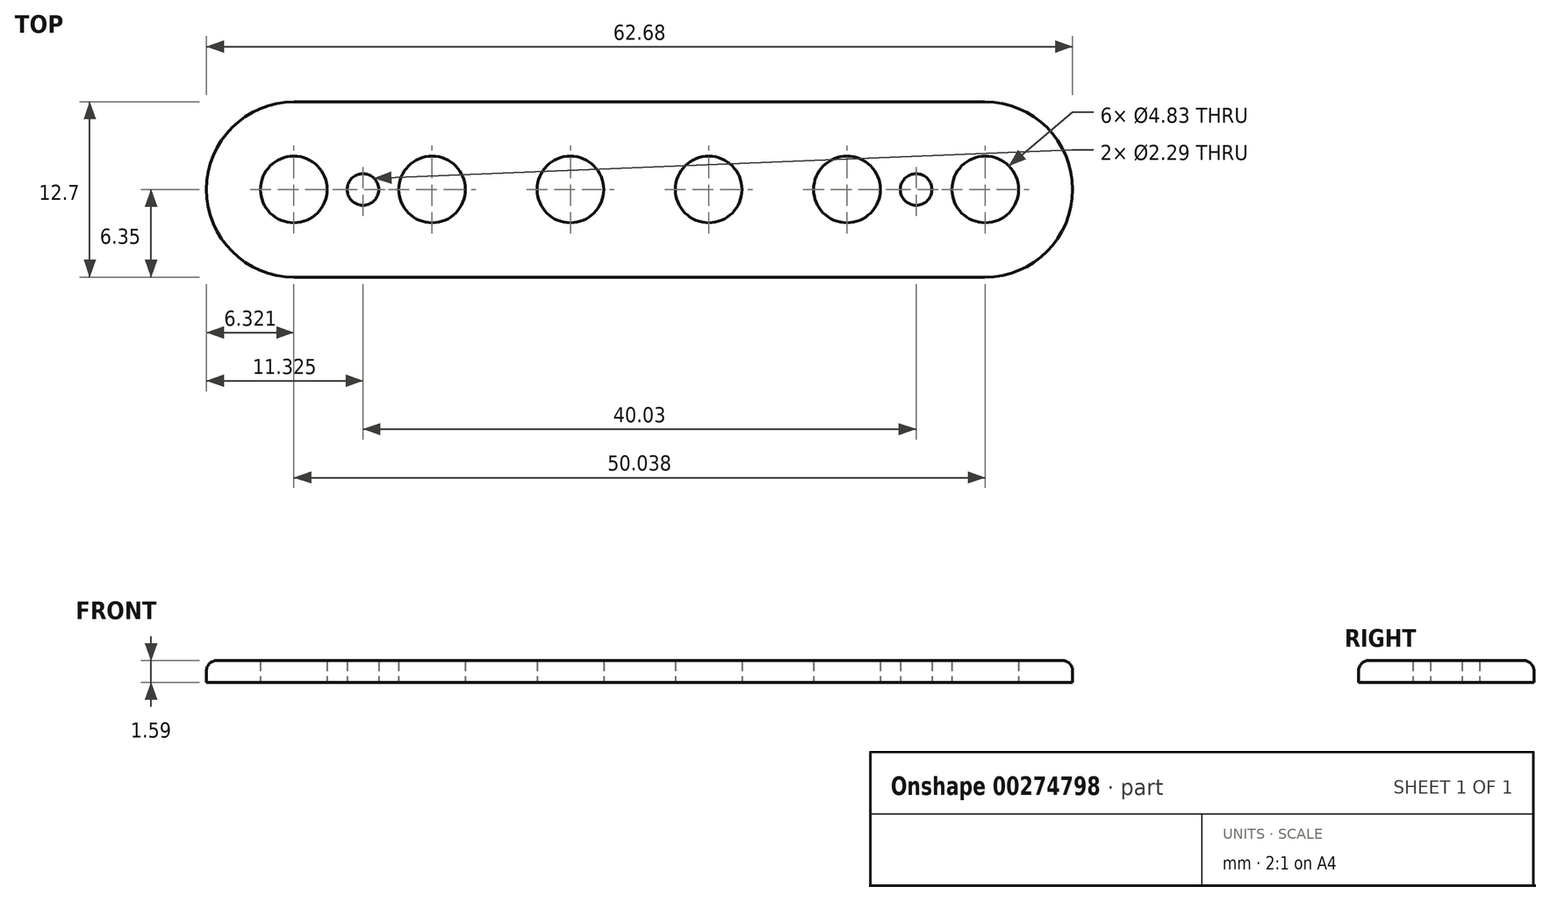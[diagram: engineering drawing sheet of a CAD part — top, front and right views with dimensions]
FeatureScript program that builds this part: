
annotation { "Feature Type Name" : "Feature", "Feature Type Description" : "" }
export const myFeature = defineFeature(function(context is Context, id is Id, definition is map)
    precondition{}
    {
        {
            var Q0;
            Q0=qCreatedBy(makeId("Top.planeOp"),FACE);
            var sketch = newSketch(context, id + "F0", { "sketchPlane" : qUnion([Q0])});
            skLineSegment(sketch, "E0", {"start": v(0, 0) * mm, "end": v(31.34, 0) * mm, "construction": true});
            skLineSegment(sketch, "E1.0", {"start": v(0, 6.35) * mm, "end": v(25, 6.35) * mm});
            skCircle(sketch, "E2", {"center": v(5, 0) * mm, "radius": 2.41 * mm});
            skCircle(sketch, "E3.1.0.0", {"center": v(15.01, 0) * mm, "radius": 2.41 * mm});
            skCircle(sketch, "E3.2.0.0", {"center": v(25.02, 0) * mm, "radius": 2.41 * mm});
            skLineSegment(sketch, "E3.direction1", {"start": v(5, 0) * mm, "end": v(15.01, 0) * mm, "construction": true});
            skLineSegment(sketch, "E4.MirrorCS", {"start": v(0, -6.35) * mm, "end": v(25, -6.35) * mm});
            skArc(sketch, "E5", {"start": v(25, -6.35) * mm, "mid": v(31.34, 0) * mm, "end": v(25, 6.35) * mm});
            skLineSegment(sketch, "E6.MirrorCS", {"start": v(0, 6.35) * mm, "end": v(-25, 6.35) * mm});
            skArc(sketch, "E7.MirrorCS", {"start": v(-25, -6.35) * mm, "mid": v(-31.34, 0) * mm, "end": v(-25, 6.35) * mm});
            skCircle(sketch, "E8.MirrorC", {"center": v(-5, 0) * mm, "radius": 2.41 * mm});
            skCircle(sketch, "E9.MirrorC", {"center": v(-25.02, 0) * mm, "radius": 2.41 * mm});
            skLineSegment(sketch, "E10.MirrorCS", {"start": v(-5, 0) * mm, "end": v(-15.01, 0) * mm, "construction": true});
            skLineSegment(sketch, "E11.MirrorCS", {"start": v(0, 0) * mm, "end": v(-31.34, 0) * mm, "construction": true});
            skCircle(sketch, "E12.MirrorC", {"center": v(-15.01, 0) * mm, "radius": 2.41 * mm});
            skLineSegment(sketch, "E13.MirrorCS", {"start": v(0, -6.35) * mm, "end": v(-25, -6.35) * mm});
            skCircle(sketch, "E14", {"center": v(20.02, 0) * mm, "radius": 1.14 * mm});
            skCircle(sketch, "E15.MirrorC", {"center": v(-20.02, 0) * mm, "radius": 1.14 * mm});
            skSolve(sketch);
        }
        {
            var Q0;
            Q0 = qSketchRegion(id + "F0", true);
            extrude(context, id + "F1", {"entities" : qUnion([Q0]), "depth" : 1.59 * mm});
        }
        {
            var Q0;
            Q0=makeQuery(id+"F1.opExtrude","CAP_EDGE",EDGE,{"disambiguationData":[OSD([sQuery(id+"F0.wireOp",EDGE,"E7.MirrorCS")])],"isStart":false});
            fillet(context, id + "F2", {"entities" : qUnion([Q0]), "radius" : 0.76 * mm, "tangentPropagation" : true, "allowEdgeOverflow" : false});
        }
    });
